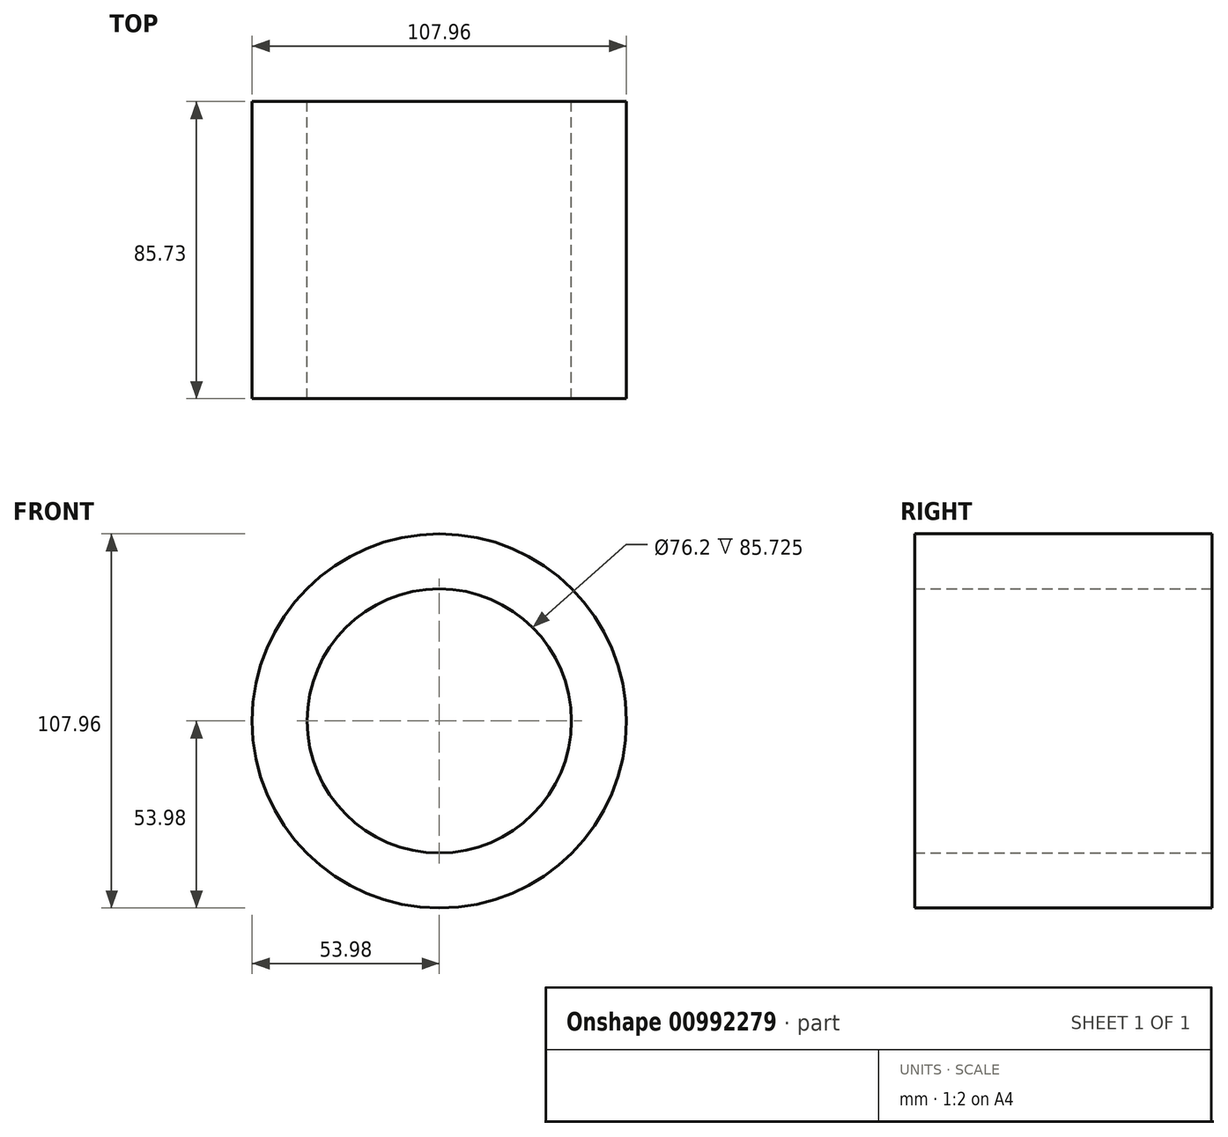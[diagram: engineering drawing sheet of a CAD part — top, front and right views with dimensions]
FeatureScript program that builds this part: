
annotation { "Feature Type Name" : "Feature", "Feature Type Description" : "" }
export const myFeature = defineFeature(function(context is Context, id is Id, definition is map)
    precondition{}
    {
        {
            var Q0;
            Q0=qCreatedBy(makeId("Front.planeOp"),FACE);
            var sketch = newSketch(context, id + "F0", { "sketchPlane" : qUnion([Q0])});
            skCircle(sketch, "E0", {"center": v(0, 0) * mm, "radius": 53.98 * mm});
            skCircle(sketch, "E1", {"center": v(0, 0) * mm, "radius": 38.1 * mm});
            skSolve(sketch);
        }
        {
            var Q0;
            Q0=makeQuery(id+"F0.imprint","IMPRINT",FACE,{"disambiguationData":[TD([[makeQuery(id+"F0.imprint","IMPRINT",EDGE,{"derivedFrom":sQuery(id+"F0.wireOp",EDGE,"E0")}),1.0]])]});
            extrude(context, id + "F1", {"entities" : qUnion([Q0]), "depth" : 85.72 * mm, "offsetDistance" : 25.4 * mm});
        }
    });
